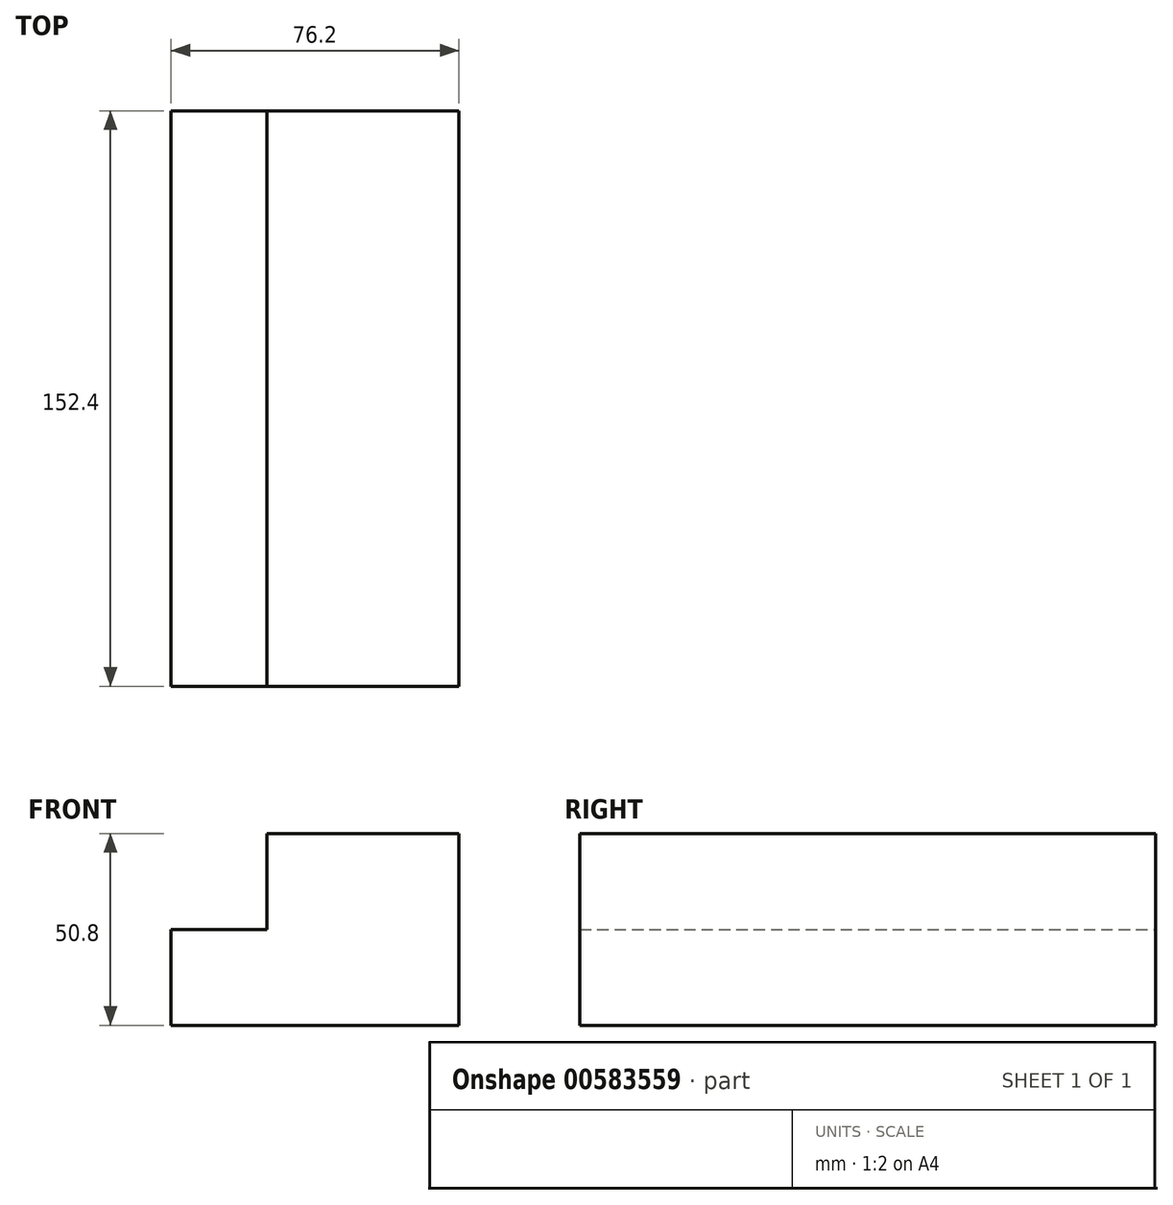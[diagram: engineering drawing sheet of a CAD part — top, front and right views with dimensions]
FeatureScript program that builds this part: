
annotation { "Feature Type Name" : "Feature", "Feature Type Description" : "" }
export const myFeature = defineFeature(function(context is Context, id is Id, definition is map)
    precondition{}
    {
        {
            var Q0;
            Q0=qCreatedBy(makeId("Front.planeOp"),FACE);
            var sketch = newSketch(context, id + "F0", { "sketchPlane" : qUnion([Q0])});
            skLineSegment(sketch, "E0", {"start": v(0, 0) * mm, "end": v(0, 25.4) * mm});
            skLineSegment(sketch, "E1", {"start": v(25.4, 25.4) * mm, "end": v(0, 25.4) * mm});
            skLineSegment(sketch, "E2", {"start": v(25.4, 25.4) * mm, "end": v(25.4, 50.8) * mm});
            skLineSegment(sketch, "E3", {"start": v(25.4, 50.8) * mm, "end": v(76.2, 50.8) * mm});
            skLineSegment(sketch, "E4", {"start": v(76.2, 0) * mm, "end": v(76.2, 50.8) * mm});
            skLineSegment(sketch, "E5", {"start": v(0, 0) * mm, "end": v(76.2, 0) * mm});
            skSolve(sketch);
        }
        {
            var Q0;
            Q0=makeQuery(id+"F0.imprint","IMPRINT",FACE,{"disambiguationData":[TD([[makeQuery(id+"F0.imprint","IMPRINT",EDGE,{"derivedFrom":sQuery(id+"F0.wireOp",EDGE,"E0")}),-1.0]])]});
            extrude(context, id + "F1", {"entities" : qUnion([Q0]), "depth" : 152.4 * mm, "offsetDistance" : 25.4 * mm});
        }
    });
